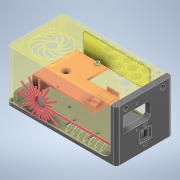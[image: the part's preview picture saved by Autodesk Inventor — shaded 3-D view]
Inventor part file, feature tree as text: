
AUTODESK INVENTOR PART (.ipt)
format: ipt  version: 2021 (Build 250183000, 183)  size: 3,105,280 bytes
history: native  units: mm
features: extrude x38, sketch x13, other x11, chamfer x9, fillet x7, boolean_combine x5, sweep x3, revolve x3, mirror x2, plane x2, pattern_linear x2, projected_geometry x2, pattern_circular x1
ambient origin geometry x8: Origin, YZ Plane, XZ Plane, XY Plane, X Axis, Y Axis, Z Axis, Center Point
bodies: Body (feature_tree), Solid3 (feature_tree), Solid4 (feature_tree), Solid8 (feature_tree), Solid10 (feature_tree), Solid12 (feature_tree), Solid13 (feature_tree), Solid14 (feature_tree)
feature tree (98):
  other  "Power Supply.ipt"
  sketch  "Sketch1"  dims[d0=10.0mm d1=27.5mm]
  extrude  "Extrusion1"  Depth=10.0mm
  extrude  "Extrusion2"  Depth=3.5mm
  sketch  "Sketch3"  dims[d2=3.5mm d3=3.5mm]
  sweep  "Sweep1"
  sweep  "Sweep2"
  sweep  "Sweep3"
  extrude  "Extrusion7"  Depth=10.5mm
  extrude  "Extrusion3"  Depth=35.0mm
  sketch  "Sketch5"  dims[d6=70.0mm d7=27.5mm]
  extrude  "Extrusion4"  Depth=13.0mm
  extrude  "Extrusion14"  Depth=29.0mm
  extrude  "Extrusion17"  Depth=4.5mm
  fillet  "Fillet3"  Radius=4.5mm
  sketch  "Sketch6"  dims[d11=27.0mm d12=77.0mm]
  extrude  "Extrusion5"  Depth=5.0mm
  mirror  "Mirror1"
  boolean_combine  "Combine1"
  extrude  "Extrusion6"  Depth=22.5mm
  mirror  "Mirror2"
  boolean_combine  "Combine2"
  fillet  "Fillet1"  Radius=28.0mm
  extrude  "Extrusion8"  Depth=5.0mm
  chamfer  "Chamfer1"  Distance=40.0mm
  sketch  "Sketch8"  dims[d15=40.0mm d16=35.0mm]
  extrude  "Extrusion9"  Depth=5.0mm
  chamfer  "Chamfer2"  Distance=3.5mm
  extrude  "Extrusion10"  Depth=5.0mm
  extrude  "Extrusion11"  Depth=5.0mm
  extrude  "Extrusion12"  Depth=5.0mm
  extrude  "Extrusion13"  Depth=5.0mm
  chamfer  "Chamfer3"  Distance=16.0mm
  fillet  "Fillet2"  Radius=7.5mm
  plane  "Work Plane1"
  other  "Laser Opening Sketch"
  revolve  "Revolution1"  [1 undecoded]
  other  "Laser Decal Sketch"
  extrude  "Extrusion15"  Depth=5.0mm
  revolve  "Revolution2"  Angle=22.5deg
  revolve  "Revolution3"  [1 undecoded]
  fillet  "Fillet5"  Radius=5.0mm
  chamfer  "4mm Chamfer"  Distance=10.0mm
  extrude  "Extrusion16"  Depth=5.0mm
  extrude  "Extrusion18"  Depth=5.0mm
  other  "Laser Warning Sketch"
  extrude  "Extrusion24"  Depth=10.0mm
  extrude  "Extrusion19"  Depth=5.0mm
  other  "USB Panel Sketch"
  extrude  "Extrusion20"  Depth=5.0mm
  extrude  "Extrusion21"  Depth=5.0mm TaperAngle=0.0deg
  extrude  "Extrusion22"  Depth=5.0mm TaperAngle=0.0deg
  chamfer  "Chamfer6"  Distance=5.0mm
  fillet  "Fillet6"  Radius=1.0mm
  extrude  "Extrusion23"  Depth=5.0mm
  chamfer  "3mm Chamfer"  Distance=1.5mm
  other  "60mm Fan Sketch"
  extrude  "Extrusion25"  Depth=5.0mm
  extrude  "Extrusion26"  Depth=5.0mm
  extrude  "Extrusion27"  Depth=5.0mm
  pattern_circular  "Circular Pattern1"  [2 undecoded]
  boolean_combine  "Combine3"
  extrude  "Extrusion28"  Depth=5.0mm
  chamfer  "Chamfer7"  Distance=2.0mm
  extrude  "Extrusion29"  TaperAngle=0.0deg  [1 undecoded]
  pattern_linear  "Rectangular Pattern1"  Spacing1=0.0mm  [1 undecoded]
  boolean_combine  "Combine4"
  other  "Logo Sketch"
  chamfer  "Chamfer8"  [1 undecoded]
  fillet  "Fillet7"  Radius=2.0mm
  plane  "Work Plane2"
  sketch  "Sketch21"  dims[d25=5.0mm d28=28.0mm]
  extrude  "Extrusion30"  Depth=5.0mm
  extrude  "Extrusion31"  Depth=5.0mm
  extrude  "Extrusion32"  Depth=5.0mm
  extrude  "Extrusion33"  Depth=5.0mm
  chamfer  "Chamfer9"  Distance=65.0mm
  extrude  "Extrusion34"  Depth=5.0mm TaperAngle=0.0deg
  fillet  "Fillet8"  Radius=15.0mm
  sketch  "Sketch22"  dims[d30=20.0mm d31=22.5mm d34=28.0mm]
  extrude  "Extrusion35"  Depth=5.0mm
  extrude  "Extrusion36"  Depth=5.0mm TaperAngle=0.0deg
  extrude  "Extrusion37"  Depth=5.0mm
  pattern_linear  "Rectangular Pattern2"  Spacing1=1.707701mm  [1 undecoded]
  boolean_combine  "Combine5"
  extrude  "Extrusion38"  TaperAngle=0.0deg  [1 undecoded]
  other  "Cover"
  sketch  "Sketch4"  dims[d4=34.0mm d5=12.5mm]
  sketch  "Sketch7"  dims[d13=66.5mm d14=10.5mm]
  projected_geometry  "Projected Loop1"
  sketch  "Sketch13"  dims[d17=13.0mm d18=13.0mm]
  sketch  "Sketch14"  dims[d19=15.5mm d21=29.0mm]
  other  "Laser Decal"
  projected_geometry  "Projected Loop2"
  other  "Laser Warning Label"
  sketch  "Sketch19"  dims[d22=4.5mm d23=4.5mm d24=4.5mm]
  other  "Driver Mount"
  sketch  "Sketch23"  dims[d35=4.5mm d36=4.5mm d37=40.0mm d39=3.5mm d40=3.5mm d41=16.0mm d43=32.7mm d44=80.1mm d45=8.0mm d46=16.0mm d47=7.5mm d48=15.0mm d49=5.0mm d52=22.5deg d56=10.0mm d58=5.0mm d59=10.0mm d60=30.0mm d61=4.0mm d62=10.0mm d63=4.0mm d64=4.0mm d65=4.0mm d66=0.0mm d69=85.0mm d70=0.0mm d71=5.0mm d72=1.0mm d74=2.0mm d75=1.5mm d76=1.5mm d77=0.25mm d78=0.25mm d79=0.25mm d80=0.25mm d81=2.0mm d82=0.0mm d83=0.0mm d84=0.0mm d85=0.0mm d86=0.0mm d87=0.0mm d88=2.0mm d89=0.0mm d91=4.0mm d92=4.0mm d93=4.75mm d94=4.75mm d95=65.0mm d96=4.0mm d97=0.0mm d98=15.0mm d99=0.25mm d100=1.5mm d101=0.0mm d102=1.707701mm d103=1.707701mm d104=0.0mm d108=0.25mm d109=0.0mm d110=14.0mm d111=2.0mm d112=0.25mm d113=0.0mm d114=1.875mm d115=2.0mm d116=45.0deg d118=15.0mm d119=85.0mm d120=4.0mm d121=4.75mm d122=4.0mm d123=4.75mm d124=65.0mm d125=6.75mm d127=4.0mm d128=0.0mm d129=5.0mm d130=3.0mm d131=15.0mm d132=45.0deg d133=4.0mm d134=0.0mm d135=3.0mm d136=0.0mm d137=3.0mm d138=0.0mm d139=3.0mm d140=0.0mm d141=1.875mm d142=10.0mm d143=45.0deg d144=3.0mm d145=8.0mm d146=3.375mm d147=8.0mm d148=5.0mm d149=3.0mm d150=6.75mm d151=3.0mm d152=0.0mm d153=5.0mm d164=26.0mm d165=90.0deg d168=1.0mm d169=0.0mm d170=0.5mm d171=1.875mm d172=10.0mm d173=45.0deg d174=1.5mm d175=10.0mm d176=45.0deg d177=15.0mm d178=15.0mm d179=15.0mm d180=15.0mm d181=15.0mm d182=15.0mm d183=15.0mm d184=15.0mm d185=15.0mm d186=15.0mm d187=15.0mm d188=15.0mm d189=15.0mm d190=15.0mm d191=15.0mm d192=15.0mm d194=4.0mm d196=1.0mm d197=0.0mm d199=3.0mm d200=0.0mm d201=28.0mm d202=48.0mm d203=17.0mm d204=45.0deg d205=45.0deg d206=12.5mm d207=17.5mm d208=10.0mm d209=0.0mm d210=24.0mm d211=40.0mm d212=3.0mm d213=3.0mm d214=110.0mm d215=30.0mm d216=2.0mm d217=2.0mm d218=2.0mm d219=2.0mm d220=2.0mm d221=3.0mm d222=10.0mm d223=0.5mm d224=0.0mm d226=21.15mm d227=14.25mm d228=39.0mm d229=3.5mm d230=3.5mm d231=30.0mm d232=12.5mm d233=11.5mm d234=20.0mm d235=20.0mm d236=2.0mm d237=0.0mm d238=5.0mm d239=0.0mm d240=2.0mm d241=0.0mm d242=2.0mm d243=2.0mm d244=45.0deg d245=2.0mm d246=0.0mm d247=0.0mm d248=5.0mm d249=90.0deg d250=3.25mm d251=1.0mm d252=0.0mm d253=60.0mm d254=60.0mm d255=57.0mm d256=5.0mm d257=5.0mm d258=20.0mm d259=5.5mm d260=5.5mm d261=5.5mm d262=5.5mm d264=0.0mm d265=0.0mm d266=1.0mm d267=0.0mm d268=1.0mm d269=0.0mm d270=1.0mm d271=0.75mm d273=1.5mm d274=0.5mm d275=110.0mm d276=360.0deg d278=2.0mm d279=50.0mm d280=1.0mm d281=0.0mm d282=4.0mm d283=2.25mm d284=2.0mm d285=45.0deg d286=60.0deg d287=3.0mm d288=3.0mm d289=3.0mm d290=10.0mm d291=1.0mm d292=0.0mm d293=70.0mm d295=10.0mm d297=0.8mm d298=90.0deg d299=0.5mm d300=2.0mm d301=45.0deg d302=5.0mm d303=51.0mm d304=6.0mm d305=1.0mm d306=1.0mm d307=1.0mm d308=1.0mm d309=1.0mm d310=1.0mm d311=69.0mm d312=76.0mm d313=68.5mm d314=3.5mm d315=3.5mm d316=55.0mm d317=15.0mm d318=40.0mm d320=110.0mm d321=9.5mm d322=0.0mm d323=17.5mm d324=0.0mm d325=1.0mm d326=0.0mm d327=1.0mm d328=1.0mm d329=1.0mm d330=1.0mm d331=1.0mm d332=1.0mm d333=2.0mm d334=0.0mm d335=3.3mm d336=2.0mm d337=45.0deg d338=5.45mm d339=5.45mm d340=2.0mm d341=2.0mm d342=2.0mm d343=2.0mm d344=2.0mm d345=2.0mm d346=2.0mm d347=0.0mm d348=5.0mm d349=40.25mm d350=1.0mm d351=1.0mm d352=0.5mm d353=0.5mm d354=3.0mm d355=0.25mm d356=0.25mm d357=2.0mm d358=2.0mm d359=1.0mm d360=1.0mm d361=1.6mm d362=1.0mm d363=20.0mm d364=0.0mm d365=6.0mm d366=4.5mm d367=3.5mm d368=3.490659mm d369=10.16mm d370=0.0mm d371=2.54mm d372=2.54mm d373=0.75mm d374=0.75mm d375=6.0mm d376=0.0mm d377=40.0mm d379=2.54mm d380=7.5mm d381=3.0mm d382=0.0mm d383=23.0mm]
note: 9 required parameter values undecoded (feature->parameter linkage not recoverable at this tier; creation-order binding heuristic only, values carry confidence <= 0.55)